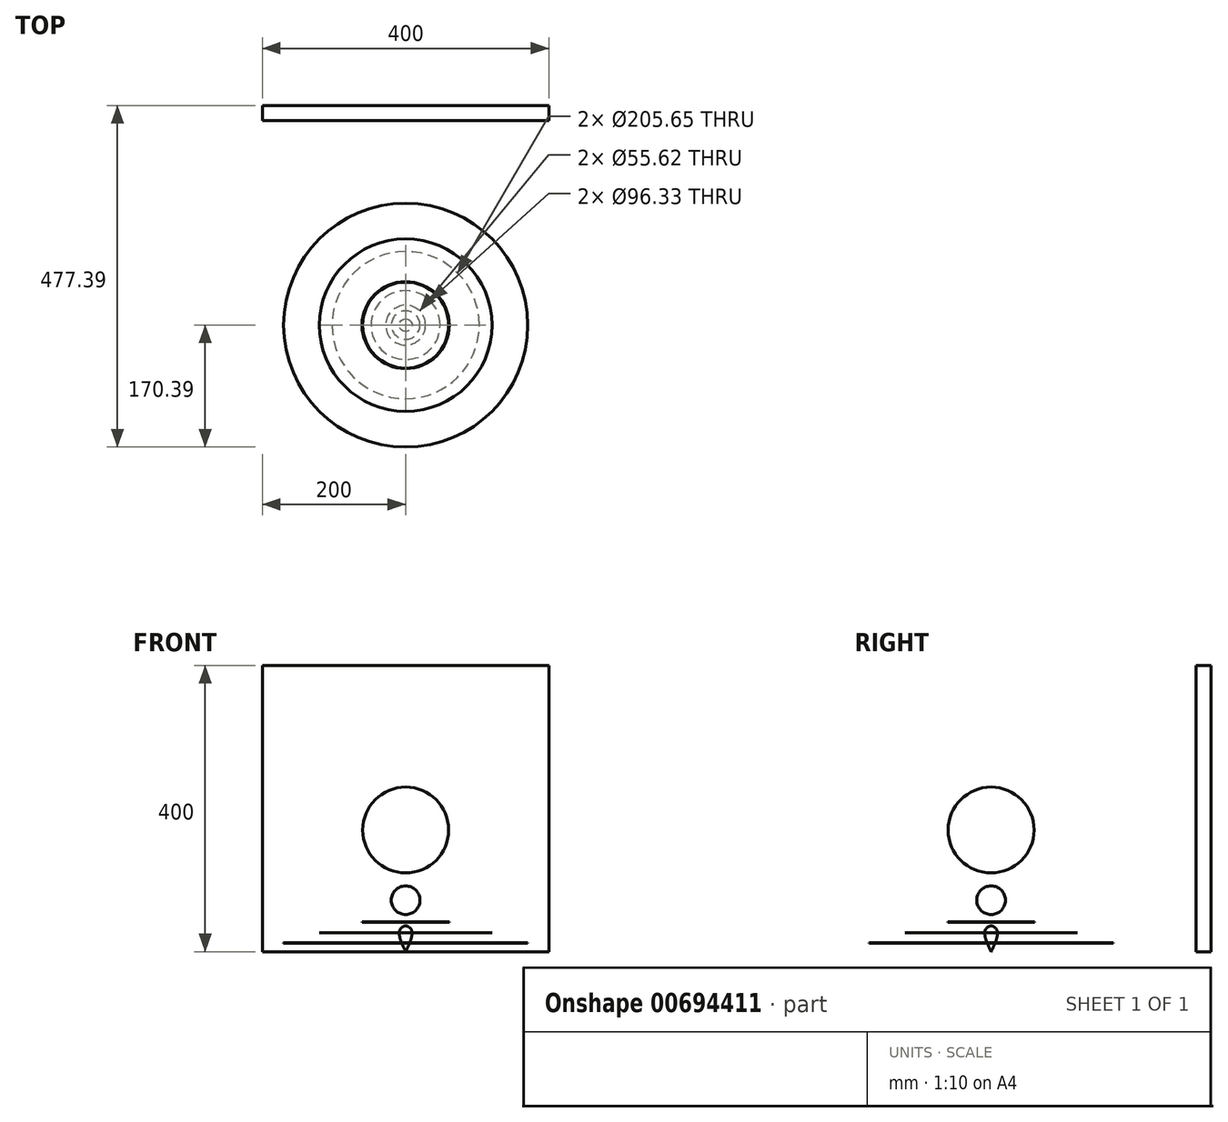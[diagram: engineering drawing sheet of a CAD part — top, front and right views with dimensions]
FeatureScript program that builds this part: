
annotation { "Feature Type Name" : "Feature", "Feature Type Description" : "" }
export const myFeature = defineFeature(function(context is Context, id is Id, definition is map)
    precondition{}
    {
        {
            var Q0;
            Q0=qCreatedBy(makeId("Front.planeOp"),FACE);
            var sketch = newSketch(context, id + "F0", { "sketchPlane" : qUnion([Q0])});
            skLineSegment(sketch, "E0.bottom", {"start": v(-200, 400) * mm, "end": v(200, 400) * mm});
            skLineSegment(sketch, "E0.top", {"start": v(-200, 0) * mm, "end": v(200, 0) * mm});
            skLineSegment(sketch, "E0.left", {"start": v(-200, 400) * mm, "end": v(-200, 0) * mm});
            skLineSegment(sketch, "E0.right", {"start": v(200, 400) * mm, "end": v(200, 0) * mm});
            skSolve(sketch);
        }
        {
            var Q0;
            Q0=qCreatedBy(makeId("Right.planeOp"),FACE);
            var sketch = newSketch(context, id + "F1", { "sketchPlane" : qUnion([Q0])});
            skLineSegment(sketch, "E1", {"start": v(-150, 230) * mm, "end": v(-150, 110) * mm});
            skArc(sketch, "E2", {"start": v(-150, 110) * mm, "mid": v(-90, 170) * mm, "end": v(-150, 230) * mm});
            skSolve(sketch);
        }
        {
            var Q0;
            Q0 = qSketchRegion(id + "F1", true);
            var Q1;
            Q1=sQuery(id+"F1.wireOp",EDGE,"E1");
            revolve(context, id + "F2", {"entities" : qUnion([Q0]), "axis" : qUnion([Q1]), "revolveType" : RevolveType.FULL});
        }
        {
            var Q0;
            Q0 = qSketchRegion(id + "F0", true);
            extrude(context, id + "F3", {"entities" : qUnion([Q0]), "oppositeDirection" : true, "depth" : 157 * mm, "offsetDistance" : 25 * mm, "hasSecondDirection" : true, "secondDirectionOppositeDirection" : true, "secondDirectionDepth" : 136 * mm});
        }
        {
            var Q0;
            Q0=qCreatedBy(makeId("Right.planeOp"),FACE);
            var sketch = newSketch(context, id + "F4", { "sketchPlane" : qUnion([Q0])});
            skFitSpline(sketch, "E3", {"points": [v(-150, 0) * mm, v(-142.62, 17.19) * mm, v(-142, 30.41) * mm, v(-150, 35.93) * mm], "startDerivative": vector(30.63, 63.93) * mm, "endDerivative": vector(-31.97, -0.45) * mm});
            skLineSegment(sketch, "E4", {"start": v(-150, 35.93) * mm, "end": v(-150, 0) * mm});
            skSolve(sketch);
        }
        {
            var Q0;
            Q0=makeQuery(id+"F4.imprint","IMPRINT",FACE,{"disambiguationData":[TD([[makeQuery(id+"F4.imprint","IMPRINT",EDGE,{"derivedFrom":sQuery(id+"F4.wireOp",EDGE,"E3")}),1.0]])]});
            var Q1;
            Q1=sQuery(id+"F4.wireOp",EDGE,"E4");
            revolve(context, id + "F5", {"entities" : qUnion([Q0]), "axis" : qUnion([Q1]), "revolveType" : RevolveType.FULL});
        }
        {
            var Q0;
            Q0=qCreatedBy(makeId("Right.planeOp"),FACE);
            var sketch = newSketch(context, id + "F6", { "sketchPlane" : qUnion([Q0])});
            skLineSegment(sketch, "E5", {"start": v(-150, 91.9) * mm, "end": v(-150, 51.9) * mm});
            skArc(sketch, "E6", {"start": v(-150, 51.9) * mm, "mid": v(-130, 71.9) * mm, "end": v(-150, 91.9) * mm});
            skSolve(sketch);
        }
        {
            var Q0;
            Q0 = qSketchRegion(id + "F6", true);
            var Q1;
            Q1=sQuery(id+"F6.wireOp",EDGE,"E5");
            revolve(context, id + "F7", {"entities" : qUnion([Q0]), "axis" : qUnion([Q1]), "revolveType" : RevolveType.FULL});
        }
        {
            var Q0;
            Q0=qCreatedBy(makeId("Right.planeOp"),FACE);
            var sketch = newSketch(context, id + "F8", { "sketchPlane" : qUnion([Q0])});
            skLineSegment(sketch, "E7", {"start": v(-150, 47.95) * mm, "end": v(-150, 0) * mm});
            skLineSegment(sketch, "E8.bottom", {"start": v(-122.2, 41.73) * mm, "end": v(-89.17, 41.73) * mm});
            skLineSegment(sketch, "E8.top", {"start": v(-122.2, 41.1) * mm, "end": v(-89.17, 41.1) * mm});
            skLineSegment(sketch, "E8.left", {"start": v(-122.2, 41.73) * mm, "end": v(-122.2, 41.1) * mm});
            skLineSegment(sketch, "E8.right", {"start": v(-89.17, 41.73) * mm, "end": v(-89.17, 41.1) * mm});
            skLineSegment(sketch, "E9.bottom", {"start": v(-101.84, 26.63) * mm, "end": v(-29.45, 26.63) * mm});
            skLineSegment(sketch, "E9.top", {"start": v(-101.84, 26.15) * mm, "end": v(-29.45, 26.15) * mm});
            skLineSegment(sketch, "E9.left", {"start": v(-101.84, 26.63) * mm, "end": v(-101.84, 26.15) * mm});
            skLineSegment(sketch, "E9.right", {"start": v(-29.45, 26.63) * mm, "end": v(-29.45, 26.15) * mm});
            skLineSegment(sketch, "E10.bottom", {"start": v(-47.18, 12.64) * mm, "end": v(20.39, 12.64) * mm});
            skLineSegment(sketch, "E10.top", {"start": v(-47.18, 12.05) * mm, "end": v(20.39, 12.05) * mm});
            skLineSegment(sketch, "E10.left", {"start": v(-47.18, 12.64) * mm, "end": v(-47.18, 12.05) * mm});
            skLineSegment(sketch, "E10.right", {"start": v(20.39, 12.64) * mm, "end": v(20.39, 12.05) * mm});
            skSolve(sketch);
        }
        {
            var Q0;
            Q0 = qSketchRegion(id + "F8", true);
            var Q1;
            Q1=sQuery(id+"F8.wireOp",EDGE,"E7");
            revolve(context, id + "F9", {"entities" : qUnion([Q0]), "axis" : qUnion([Q1]), "revolveType" : RevolveType.FULL});
        }
        {
            var Q0;
            Q0 = qSketchRegion(id + "F8", true);
            var Q1;
            Q1=makeQuery(id+"F5.opRevolve","SWEPT_FACE",FACE,{"disambiguationData":[OSD([sQuery(id+"F4.wireOp",EDGE,"E3")])]});
            revolve(context, id + "F10", {"entities" : qUnion([Q0]), "axis" : qUnion([Q1]), "revolveType" : RevolveType.FULL});
        }
    });
